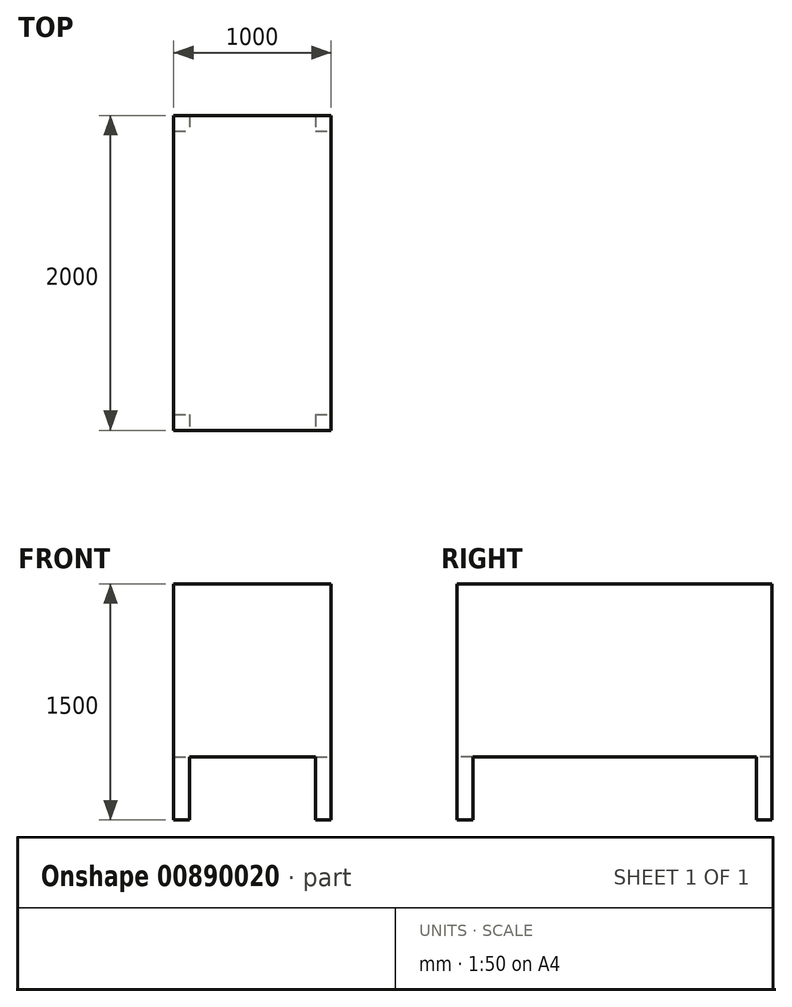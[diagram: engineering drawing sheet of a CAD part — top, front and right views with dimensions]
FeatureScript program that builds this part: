
annotation { "Feature Type Name" : "Feature", "Feature Type Description" : "" }
export const myFeature = defineFeature(function(context is Context, id is Id, definition is map)
    precondition{}
    {
        {
            var Q0;
            Q0=qCreatedBy(makeId("Top.planeOp"),FACE);
            var sketch = newSketch(context, id + "F0", { "sketchPlane" : qUnion([Q0])});
            skLineSegment(sketch, "E0", {"start": v(0, 0) * mm, "end": v(0, 2000) * mm});
            skLineSegment(sketch, "E1", {"start": v(0, 2000) * mm, "end": v(-1000, 2000) * mm});
            skLineSegment(sketch, "E2", {"start": v(-1000, 2000) * mm, "end": v(-1000, 0) * mm});
            skLineSegment(sketch, "E3", {"start": v(-1000, 0) * mm, "end": v(0, 0) * mm});
            skSolve(sketch);
        }
        {
            var Q0;
            Q0 = qSketchRegion(id + "F0", true);
            extrude(context, id + "F1", {"entities" : qUnion([Q0]), "depth" : 1500 * mm, "offsetDistance" : 25 * mm});
        }
        {
            var Q0;
            Q0=makeQuery(id+"F1.opExtrude","SWEPT_FACE",FACE,{"disambiguationData":[OSD([sQuery(id+"F0.wireOp",EDGE,"E3")])]});
            var sketch = newSketch(context, id + "F2", { "sketchPlane" : qUnion([Q0])});
            skLineSegment(sketch, "E4", {"start": v(-1000, 0) * mm, "end": v(-900, 0) * mm});
            skLineSegment(sketch, "E5", {"start": v(-900, 0) * mm, "end": v(-900, 400) * mm});
            skLineSegment(sketch, "E6", {"start": v(0, 0) * mm, "end": v(-100, 0) * mm});
            skLineSegment(sketch, "E7", {"start": v(-100, 0) * mm, "end": v(-100, 400) * mm});
            skLineSegment(sketch, "E8", {"start": v(-100, 400) * mm, "end": v(-900, 400) * mm});
            skSolve(sketch);
        }
        {
            var Q0;
            {var subQ0=sQuery(id+"F2.wireOp",EDGE,"E5");Q0=makeQuery(id+"F2.imprint","IMPRINT",FACE,{"disambiguationData":[TD([[makeQuery(id+"F2.imprint","IMPRINT",EDGE,{"derivedFrom":subQ0}),-1.0]])]});}
            extrude(context, id + "F3", {"entities" : qUnion([Q0]), "operationType" : NewBodyOperationType.REMOVE, "oppositeDirection" : true, "depth" : 2000 * mm, "offsetDistance" : 25 * mm});
        }
        {
            var Q0;
            Q0=makeQuery(id+"F1.opExtrude","SWEPT_FACE",FACE,{"disambiguationData":[OSD([sQuery(id+"F0.wireOp",EDGE,"E0")])]});
            var sketch = newSketch(context, id + "F4", { "sketchPlane" : qUnion([Q0])});
            skLineSegment(sketch, "E9", {"start": v(0, 0) * mm, "end": v(100, 0) * mm});
            skLineSegment(sketch, "E10", {"start": v(100, 0) * mm, "end": v(100, 400) * mm});
            skLineSegment(sketch, "E11", {"start": v(100, 400) * mm, "end": v(1900, 400) * mm});
            skLineSegment(sketch, "E12", {"start": v(1900, 400) * mm, "end": v(1900, 0) * mm});
            skSolve(sketch);
        }
        {
            var Q0;
            {var subQ0=sQuery(id+"F4.wireOp",EDGE,"E10");Q0=makeQuery(id+"F4.imprint","IMPRINT",FACE,{"disambiguationData":[TD([[makeQuery(id+"F4.imprint","IMPRINT",EDGE,{"derivedFrom":subQ0}),-1.0]])]});}
            extrude(context, id + "F5", {"entities" : qUnion([Q0]), "operationType" : NewBodyOperationType.REMOVE, "oppositeDirection" : true, "depth" : 1000 * mm, "offsetDistance" : 25 * mm});
        }
    });
